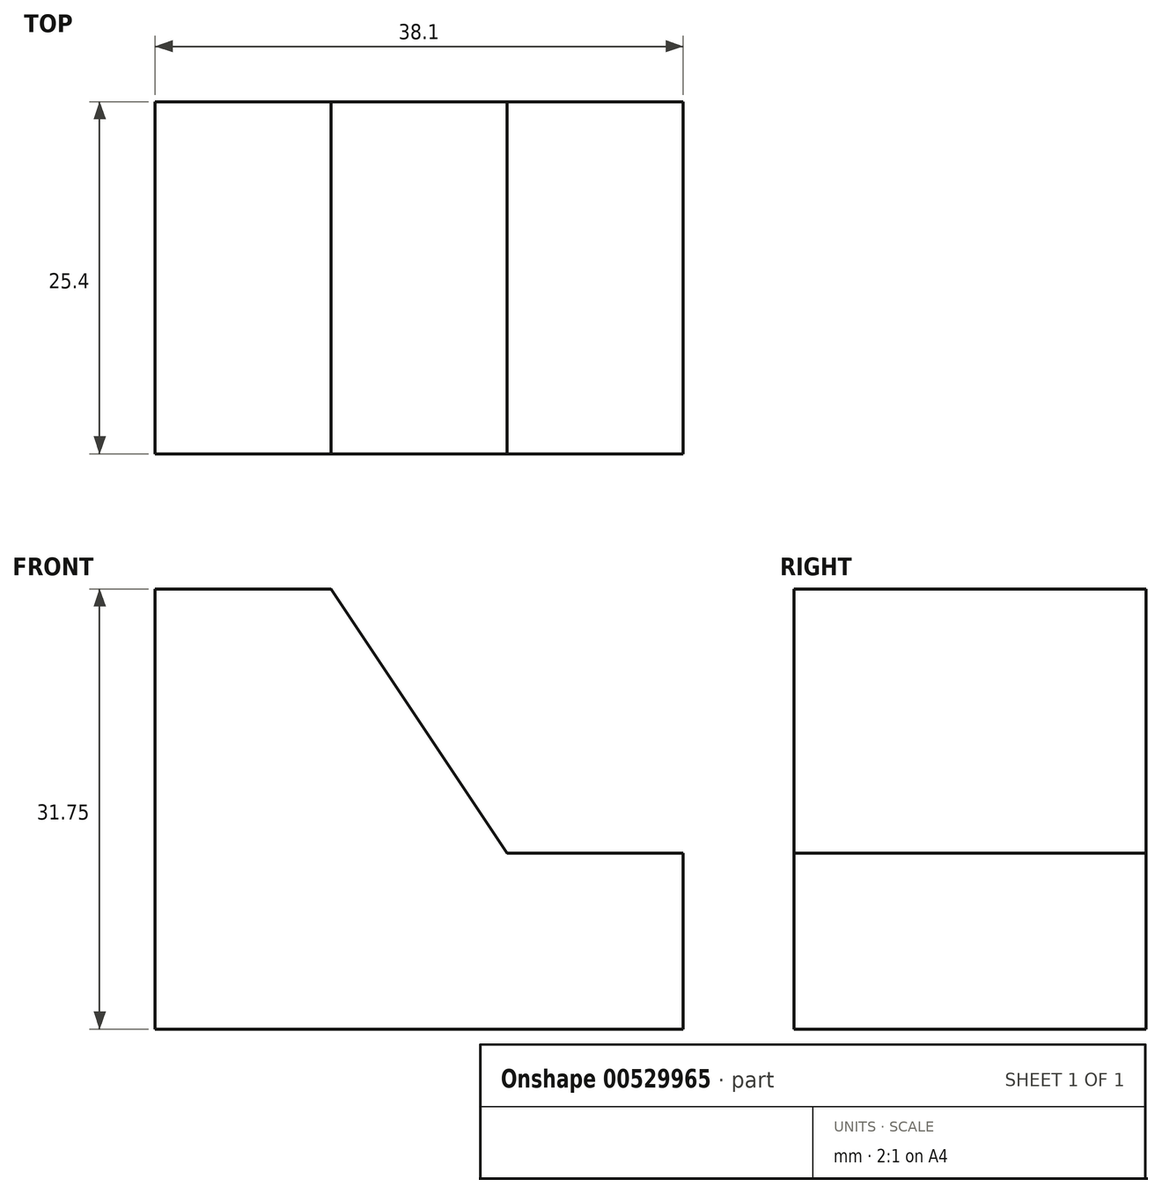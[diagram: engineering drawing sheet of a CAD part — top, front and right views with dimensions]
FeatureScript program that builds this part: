
annotation { "Feature Type Name" : "Feature", "Feature Type Description" : "" }
export const myFeature = defineFeature(function(context is Context, id is Id, definition is map)
    precondition{}
    {
        {
            var Q0;
            Q0=qCreatedBy(makeId("Front.planeOp"),FACE);
            var sketch = newSketch(context, id + "F0", { "sketchPlane" : qUnion([Q0])});
            skLineSegment(sketch, "E0", {"start": v(-71.83, 49.97) * mm, "end": v(-71.83, 18.22) * mm});
            skLineSegment(sketch, "E1", {"start": v(-71.83, 18.22) * mm, "end": v(-33.73, 18.22) * mm});
            skLineSegment(sketch, "E2", {"start": v(-33.73, 18.22) * mm, "end": v(-33.73, 30.92) * mm});
            skLineSegment(sketch, "E3", {"start": v(-33.73, 30.92) * mm, "end": v(-46.43, 30.92) * mm});
            skLineSegment(sketch, "E4", {"start": v(-71.83, 49.97) * mm, "end": v(-59.13, 49.97) * mm});
            skLineSegment(sketch, "E5", {"start": v(-46.43, 30.92) * mm, "end": v(-59.13, 49.97) * mm});
            skSolve(sketch);
        }
        {
            var Q0;
            Q0 = qSketchRegion(id + "F0", true);
            extrude(context, id + "F1", {"entities" : qUnion([Q0]), "depth" : 25.4 * mm, "offsetDistance" : 25.4 * mm});
        }
    });
